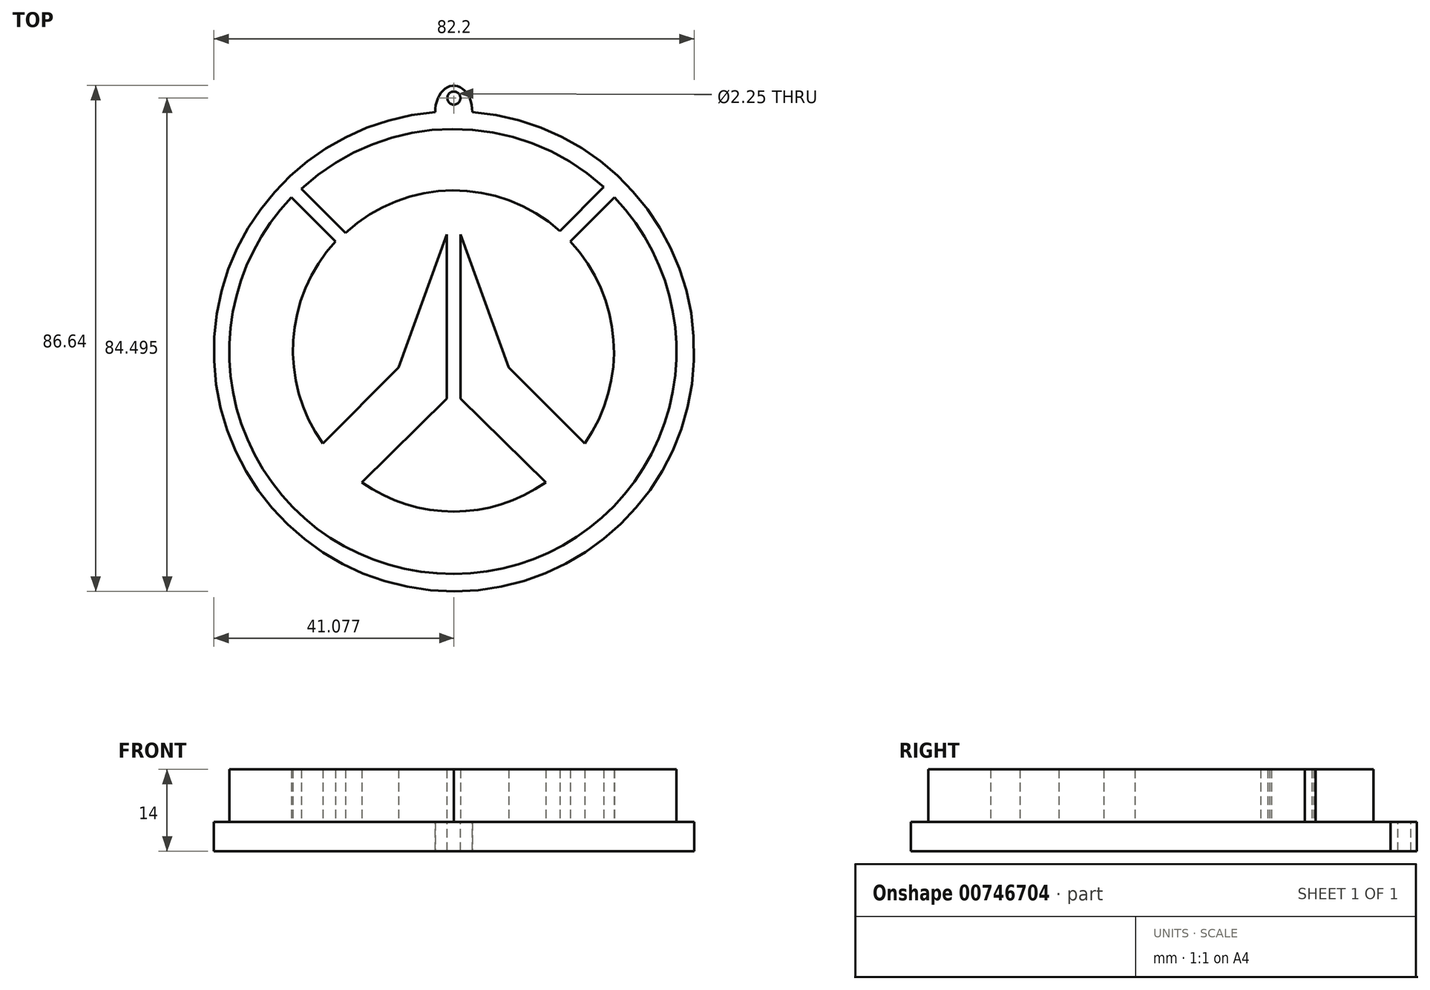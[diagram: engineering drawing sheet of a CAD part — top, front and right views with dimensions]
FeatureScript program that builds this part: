
annotation { "Feature Type Name" : "Feature", "Feature Type Description" : "" }
export const myFeature = defineFeature(function(context is Context, id is Id, definition is map)
    precondition{}
    {
        {
            var Q0;
            Q0=qCreatedBy(makeId("Top.planeOp"),FACE);
            var sketch = newSketch(context, id + "F0", { "sketchPlane" : qUnion([Q0])});
            skArc(sketch, "E0", {"start": v(25.67, 27.45) * mm, "mid": v(-0.26, 37.38) * mm, "end": v(-26.07, 27.13) * mm});
            skLineSegment(sketch, "E1", {"start": v(25.67, 27.45) * mm, "end": v(18.2, 19.89) * mm});
            skLineSegment(sketch, "E2", {"start": v(-26.07, 27.13) * mm, "end": v(-18.51, 19.6) * mm});
            skArc(sketch, "E3", {"start": v(18.2, 19.89) * mm, "mid": v(-0.21, 26.85) * mm, "end": v(-18.51, 19.6) * mm});
            skArc(sketch, "E4", {"start": v(0, -38.82) * mm, "mid": v(35.07, -15.68) * mm, "end": v(27.5, 25.65) * mm});
            skArc(sketch, "E5", {"start": v(-27.79, 25.65) * mm, "mid": v(-35.33, -15.82) * mm, "end": v(0, -38.82) * mm});
            skArc(sketch, "E6", {"start": v(-20.26, 18.09) * mm, "mid": v(-27.49, 1.17) * mm, "end": v(-22.42, -16.5) * mm});
            skArc(sketch, "E7", {"start": v(-15.74, -23.16) * mm, "mid": v(0, -28.16) * mm, "end": v(15.74, -23.16) * mm});
            skArc(sketch, "E8", {"start": v(22.41, -16.5) * mm, "mid": v(27.34, 1.23) * mm, "end": v(19.97, 18.09) * mm});
            skLineSegment(sketch, "E9", {"start": v(-27.79, 25.65) * mm, "end": v(-20.26, 18.09) * mm});
            skLineSegment(sketch, "E10", {"start": v(-22.42, -16.5) * mm, "end": v(-9.44, -3.48) * mm});
            skLineSegment(sketch, "E11", {"start": v(-9.44, -3.48) * mm, "end": v(-1.17, 19.3) * mm});
            skLineSegment(sketch, "E12", {"start": v(-1.17, 19.3) * mm, "end": v(-1.17, -8.82) * mm});
            skLineSegment(sketch, "E13", {"start": v(-15.74, -23.16) * mm, "end": v(-1.17, -8.82) * mm});
            skLineSegment(sketch, "E14", {"start": v(1.16, -8.82) * mm, "end": v(15.74, -23.16) * mm});
            skLineSegment(sketch, "E15", {"start": v(1.16, -8.82) * mm, "end": v(1.16, 19.3) * mm});
            skLineSegment(sketch, "E16", {"start": v(1.16, 19.3) * mm, "end": v(9.43, -3.48) * mm});
            skLineSegment(sketch, "E17", {"start": v(9.43, -3.48) * mm, "end": v(22.41, -16.5) * mm});
            skLineSegment(sketch, "E18", {"start": v(19.97, 18.09) * mm, "end": v(27.5, 25.65) * mm});
            skSolve(sketch);
        }
        {
            var Q0;
            Q0=makeQuery(id+"F0.imprint","IMPRINT",FACE,{"disambiguationData":[TD([[makeQuery(id+"F0.imprint","IMPRINT",EDGE,{"derivedFrom":sQuery(id+"F0.wireOp",EDGE,"E4")}),1.0]])]});
            var Q1;
            Q1=makeQuery(id+"F0.imprint","IMPRINT",FACE,{"disambiguationData":[TD([[makeQuery(id+"F0.imprint","IMPRINT",EDGE,{"derivedFrom":sQuery(id+"F0.wireOp",EDGE,"E0")}),1.0]])]});
            extrude(context, id + "F1", {"entities" : qUnion([Q0, Q1]), "depth" : 9 * mm});
        }
        {
            var Q0;
            Q0=qCreatedBy(makeId("Top.planeOp"),FACE);
            var sketch = newSketch(context, id + "F2", { "sketchPlane" : qUnion([Q0])});
            skCircle(sketch, "E19", {"center": v(0.04, -0.72) * mm, "radius": 41.1 * mm});
            skEllipse(sketch, "E20", {"center": v(0, 40.38) * mm, "majorRadius": 4.44 * mm, "minorRadius": 3.16 * mm, "majorAxis": v(0, -1)});
            skCircle(sketch, "E21", {"center": v(0.02, 42.67) * mm, "radius": 1.13 * mm});
            skSolve(sketch);
        }
        {
            var Q0;
            Q0=qSketchRegion(id+"F2",true);
            extrude(context, id + "F3", {"entities" : qUnion([Q0]), "oppositeDirection" : true, "depth" : 5 * mm});
        }
    });
